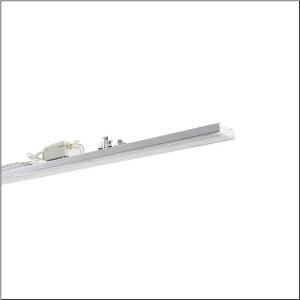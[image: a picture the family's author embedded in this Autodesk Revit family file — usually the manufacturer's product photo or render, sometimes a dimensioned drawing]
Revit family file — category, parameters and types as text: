
# Revit family: licross_21_recessed_mo_52te18dv4e5g
name_source: partatom
category: Lighting Fixtures
units: mm (PartAtom-declared; Revit-internal decimal feet)

## family parameters
Cut with Voids When Loaded = No
Host = Face
Light Source = No
Part Type = Normal
Room Calculation Point = No
Round Connector Dimension = Use Diameter
Shared = No

## types (1)
- --- (1 x LED, 14980 lm, 85.3 W, 4000K)
    Apparent Load = 85 VA
    CIE Flux Codes = 79 95 99 100 100
    Color Rendering = 80
    Color Temperature = 4000K
    Default Elevation = 1800 mm
    Description = Licross 21 Recessed MO, luminaire insert, of sheet steel, galvanised, coil coated, white, length: 2.250mm, width: 66mm, height: 67mm, LED rated luminous flux: 14.980lm, light colour: 840, SDCM (Standard Deviation of Colour Matching)MacAdam ≤ 3 SDCM (initial), control gear: DALI 2, with plug, 5-pole, with phase selection, mains connection: 220..240V, AC, 50/60Hz, rated input power: 85W, internal wiring halogen-free, primary light control with lens, of plastic, primary optical cover: cover, of PMMA, light emission: direct distribution, primary light characteristic: symmetric, protection rating (complete): IP54, insulation class (complete): insulation class I (protective earthing), certification: CE, ENEC, VDE, UKCA, protection symbol: D if used in an environment with non-conductive dust loads with corresponding accessories, impact resistance: IK06, permissible ambient temperature for indoor applications: -25..+35°C, corresponds to IFS (International Featured Standards) requirements for safety and quality in the food industry, reducing of maximum allowable ambient temperature of 5°C with ceiling mounting, LABS conformity tested according to VDMA 24364:2018-05, The light source and the operating device comply with the requirements of the Ecodesign Regulation (EU) 2019/2020 and are replaceable in accordance with this regulation, packaging unit: 1 piece
    Height = 58 mm
    Lamp = 1 x LED
    Lamp Light Flux = 14980 lm
    Lamp Power = 85.3 W
    Lamp count = 1
    Length = 2250 mm
    Luminous efficacy = 176 lm/W
    Manufacturer = Siteco
    ModVariant = No
    Model = 52TE18DV4E5G
    Mounting Place = Ceiling
    Mounting Type = Pendant
    Number of Poles = 1
    OnlyDefault = Yes
    Power Factor = 1
    Product Name = Licross 21 Recessed MO
    Product group = luminaire insert | ceiling pendant
    ProductGroupID = 901
    Protection Class = Protection class I
    Protection Degree = IP 54
    RLX_Detail_Level = 1
    RLX_Emergency_Light_Flux = 0 lm
    RLX_Emergency_Type = 0
    RLX_Emergency_Type_DB = No
    RlxData = <blob elided: 29817 chars, md5=c0e84c74>
    Socket = socket
    Standby Power = 0 W
    System Light Flux = 14980 lm
    System Power = 85 W
    Type Comments = factory setting: luminous flux: 100 % | dim-lin: 254 | 390 mA
    Type Image = l_1296930.jpg
    URL = http://relux.com
    VarID = @adj_127731
    Voltage = 0 V
    Weight = 0.00 kg
    Width = 66 mm

## geometry (parser evidence)
native form markers: Blend x4, Sweep x10
no freeform markers — native parametric forms only
